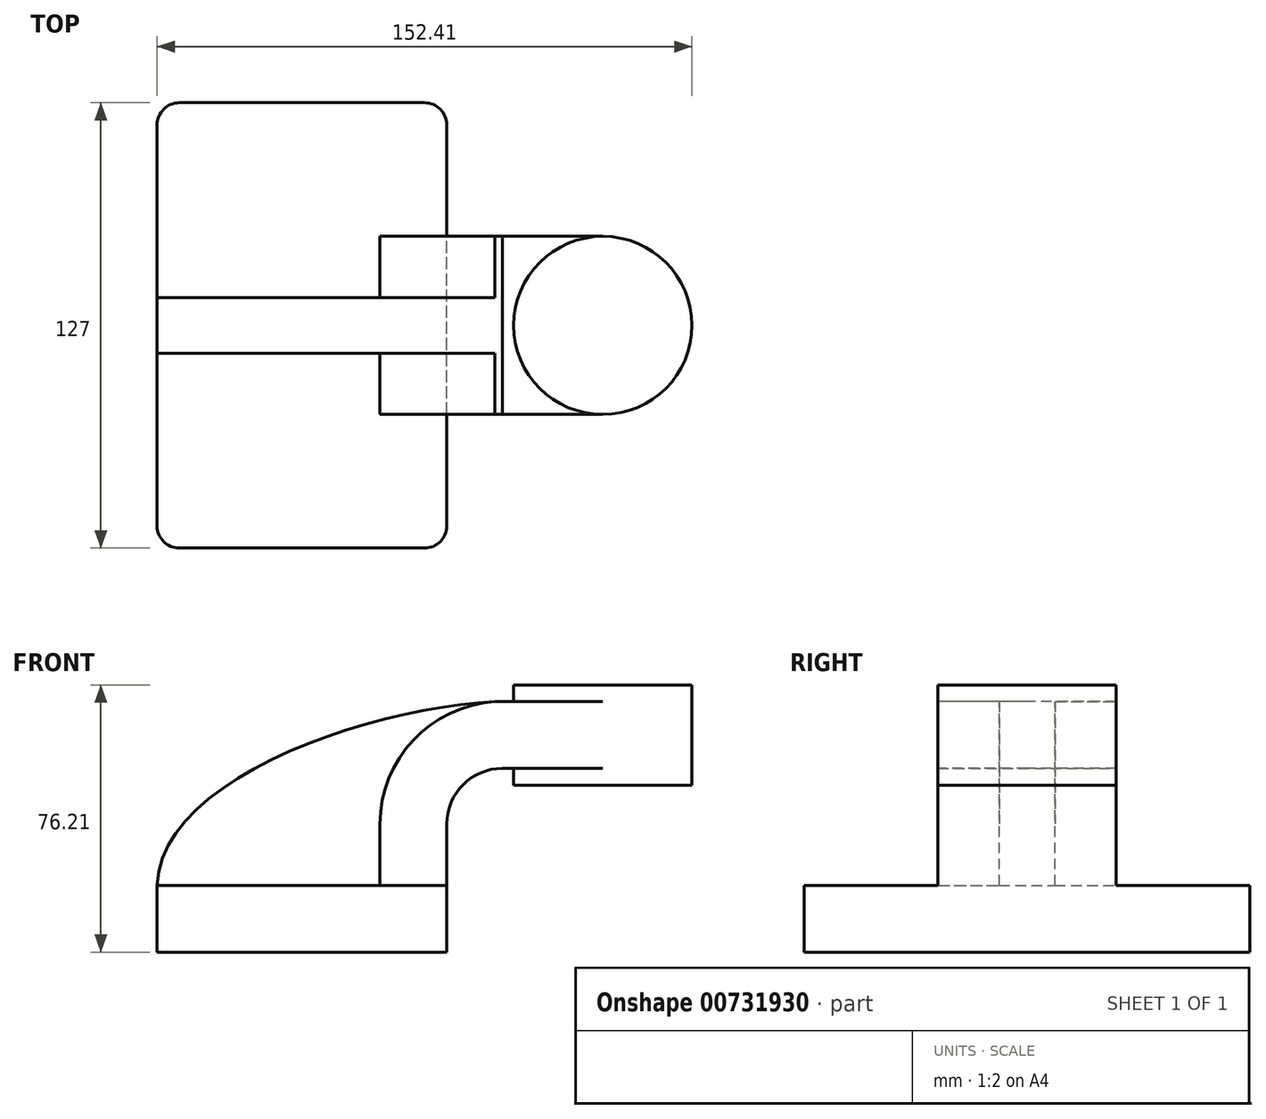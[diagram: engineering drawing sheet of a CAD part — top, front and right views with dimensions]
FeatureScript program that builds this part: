
annotation { "Feature Type Name" : "Feature", "Feature Type Description" : "" }
export const myFeature = defineFeature(function(context is Context, id is Id, definition is map)
    precondition{}
    {
        {
            var Q0;
            Q0=qCreatedBy(makeId("Front.planeOp"),FACE);
            var sketch = newSketch(context, id + "F0", { "sketchPlane" : qUnion([Q0])});
            skLineSegment(sketch, "E0.bottom", {"start": v(41.28, -9.52) * mm, "end": v(-41.28, -9.53) * mm});
            skLineSegment(sketch, "E0.top", {"start": v(41.28, 9.53) * mm, "end": v(-41.28, 9.53) * mm});
            skLineSegment(sketch, "E0.left", {"start": v(41.28, -9.52) * mm, "end": v(41.28, 9.53) * mm});
            skLineSegment(sketch, "E0.right", {"start": v(-41.28, -9.53) * mm, "end": v(-41.28, 9.53) * mm});
            skPoint(sketch, "E0.middle", {"position": v(0, 0) * mm});
            skLineSegment(sketch, "E1.bottom", {"start": v(60.33, 38.1) * mm, "end": v(111.12, 38.1) * mm});
            skLineSegment(sketch, "E1.top", {"start": v(60.32, 66.68) * mm, "end": v(111.12, 66.68) * mm});
            skLineSegment(sketch, "E1.left", {"start": v(60.32, 38.1) * mm, "end": v(60.32, 66.68) * mm});
            skLineSegment(sketch, "E1.right", {"start": v(111.12, 38.1) * mm, "end": v(111.12, 66.68) * mm});
            skPoint(sketch, "E1.middle", {"position": v(85.72, 52.39) * mm});
            skLineSegment(sketch, "E2", {"start": v(41.28, 9.53) * mm, "end": v(41.28, 27) * mm});
            skArc(sketch, "E3", {"start": v(41.27, 27) * mm, "mid": v(45.92, 38.23) * mm, "end": v(57.15, 42.88) * mm});
            skLineSegment(sketch, "E4", {"start": v(57.15, 42.88) * mm, "end": v(85.72, 42.88) * mm});
            skLineSegment(sketch, "E5.0", {"start": v(57.15, 61.93) * mm, "end": v(85.72, 61.93) * mm});
            skArc(sketch, "E5.1", {"start": v(22.23, 27) * mm, "mid": v(32.45, 51.7) * mm, "end": v(57.15, 61.93) * mm});
            skLineSegment(sketch, "E5.2", {"start": v(22.22, 9.53) * mm, "end": v(22.22, 27) * mm});
            skLineSegment(sketch, "E6", {"start": v(85.72, 38.1) * mm, "end": v(85.72, 66.68) * mm});
            skFitSpline(sketch, "E7", {"points": [v(-41.28, 9.52) * mm, v(57.15, 61.93) * mm], "startDerivative": vector(2.1, 92.66) * mm, "endDerivative": vector(105.83, 2.1) * mm});
            skSolve(sketch);
        }
        {
            var Q0;
            Q0=makeQuery(id+"F0.imprint","IMPRINT",FACE,{"disambiguationData":[TD([[makeQuery(id+"F0.imprint","IMPRINT",EDGE,{"derivedFrom":sQuery(id+"F0.wireOp",EDGE,"E0.bottom")}),-1.0]])]});
            extrude(context, id + "F1", {"entities" : qUnion([Q0]), "endBound" : BoundingType.SYMMETRIC, "depth" : 127 * mm, "offsetDistance" : 25.4 * mm});
        }
        {
            var Q0;
            {var subQ0=sQuery(id+"F0.wireOp",EDGE,"E4");var subQ1=sQuery(id+"F0.wireOp",EDGE,"E1.left");var subQ2=makeQuery(id+"F0.imprint","INTERSECT",VERTEX,{"derivedFrom":[subQ1,subQ0]});Q0=makeQuery(id+"F0.imprint","IMPRINT",FACE,{"disambiguationData":[TD([[makeQuery(id+"F0.imprint","IMPRINT",EDGE,{"disambiguationData":[TD([[subQ2,-1.0]])],"derivedFrom":subQ1}),-1.0]])]});}
            var Q1;
            {var subQ1=sQuery(id+"F0.wireOp",EDGE,"E2");Q1=makeQuery(id+"F0.imprint","IMPRINT",FACE,{"disambiguationData":[TD([[makeQuery(id+"F0.imprint","IMPRINT",EDGE,{"derivedFrom":subQ1}),1.0]])]});}
            extrude(context, id + "F2", {"entities" : qUnion([Q0, Q1]), "operationType" : NewBodyOperationType.ADD, "endBound" : BoundingType.SYMMETRIC, "depth" : 50.8 * mm, "offsetDistance" : 25.4 * mm});
        }
        {
            var Q0;
            {var subQ3=sQuery(id+"F0.wireOp",EDGE,"E5.2");Q0=makeQuery(id+"F0.imprint","IMPRINT",FACE,{"disambiguationData":[TD([[makeQuery(id+"F0.imprint","IMPRINT",EDGE,{"derivedFrom":subQ3}),1.0]])]});}
            extrude(context, id + "F3", {"entities" : qUnion([Q0]), "operationType" : NewBodyOperationType.ADD, "endBound" : BoundingType.SYMMETRIC, "depth" : 15.88 * mm, "offsetDistance" : 25.4 * mm});
        }
        {
            var Q0;
            {var subQ4=sQuery(id+"F0.wireOp",EDGE,"E1.right");Q0=makeQuery(id+"F0.imprint","IMPRINT",FACE,{"disambiguationData":[TD([[makeQuery(id+"F0.imprint","IMPRINT",EDGE,{"derivedFrom":subQ4}),1.0]])]});}
            var Q1;
            Q1=sQuery(id+"F0.wireOp",EDGE,"E6");
            revolve(context, id + "F4", {"operationType" : NewBodyOperationType.ADD, "surfaceOperationType" : NewSurfaceOperationType.NEW, "entities" : qUnion([Q0]), "axis" : qUnion([Q1]), "revolveType" : RevolveType.FULL});
        }
        {
            var Q0;
            Q0=makeQuery(id+"F1.opExtrude","CAP_EDGE",EDGE,{"disambiguationData":[OSD([sQuery(id+"F0.wireOp",EDGE,"E0.left")])],"isStart":false});
            var Q1;
            Q1=makeQuery(id+"F1.opExtrude","CAP_EDGE",EDGE,{"disambiguationData":[OSD([sQuery(id+"F0.wireOp",EDGE,"E0.right")])],"isStart":false});
            var Q2;
            Q2=makeQuery(id+"F1.opExtrude","CAP_EDGE",EDGE,{"disambiguationData":[OSD([sQuery(id+"F0.wireOp",EDGE,"E0.left")])],"isStart":true});
            var Q3;
            Q3=makeQuery(id+"F1.opExtrude","CAP_EDGE",EDGE,{"disambiguationData":[OSD([sQuery(id+"F0.wireOp",EDGE,"E0.right")])],"isStart":true});
            fillet(context, id + "F5", {"entities" : qUnion([Q0, Q1, Q2, Q3]), "radius" : 6.35 * mm, "tangentPropagation" : true, "allowEdgeOverflow" : false});
        }
    });
